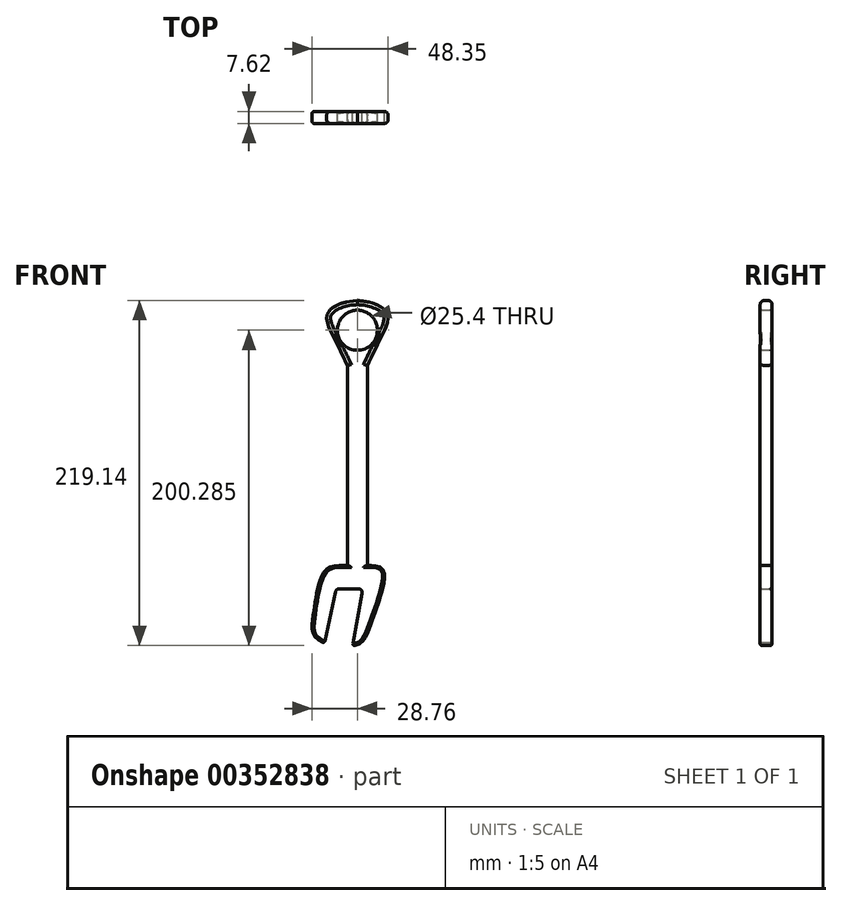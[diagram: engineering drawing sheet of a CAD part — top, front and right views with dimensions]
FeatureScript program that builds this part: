
annotation { "Feature Type Name" : "Feature", "Feature Type Description" : "" }
export const myFeature = defineFeature(function(context is Context, id is Id, definition is map)
    precondition{}
    {
        {
            var Q0;
            Q0=qCreatedBy(makeId("Front.planeOp"),FACE);
            var sketch = newSketch(context, id + "F0", { "sketchPlane" : qUnion([Q0])});
            skLineSegment(sketch, "E0.bottom", {"start": v(-6.35, 63.5) * mm, "end": v(6.35, 63.5) * mm});
            skLineSegment(sketch, "E0.top", {"start": v(-6.35, -63.5) * mm, "end": v(6.35, -63.5) * mm});
            skLineSegment(sketch, "E0.left", {"start": v(-6.35, 63.5) * mm, "end": v(-6.35, -63.5) * mm});
            skLineSegment(sketch, "E0.right", {"start": v(6.35, 63.5) * mm, "end": v(6.35, -63.5) * mm});
            skPoint(sketch, "E0.middle", {"position": v(0, 0) * mm});
            skLineSegment(sketch, "E1", {"start": v(-20.84, -113.07) * mm, "end": v(-13.93, -80.42) * mm});
            skLineSegment(sketch, "E2", {"start": v(-11.44, -78.4) * mm, "end": v(0.55, -78.4) * mm});
            skLineSegment(sketch, "E3", {"start": v(3.04, -81.41) * mm, "end": v(-3.28, -114.85) * mm});
            skFitSpline(sketch, "E4", {"points": [v(-3.28, -114.85) * mm, v(2.72, -112.4) * mm, v(10.94, -94.4) * mm, v(16.5, -66.62) * mm, v(6.35, -63.5) * mm], "startDerivative": vector(38.66, 7.37) * mm, "endDerivative": vector(-61.43, 0.88) * mm});
            skFitSpline(sketch, "E5", {"points": [v(-6.35, -63.5) * mm, v(-19.73, -66.18) * mm, v(-25.95, -82.18) * mm, v(-28.4, -98.18) * mm, v(-27.73, -107.96) * mm, v(-20.84, -113.07) * mm], "startDerivative": vector(-73.53, 0.95) * mm, "endDerivative": vector(51.22, -25.64) * mm});
            skPoint(sketch, "E6.visualSharp", {"position": v(-13.5, -78.4) * mm});
            skArc(sketch, "E6.filletArc", {"start": v(-11.44, -78.4) * mm, "mid": v(-13.04, -78.97) * mm, "end": v(-13.93, -80.42) * mm});
            skPoint(sketch, "E7.visualSharp", {"position": v(3.61, -78.4) * mm});
            skArc(sketch, "E7.filletArc", {"start": v(3.04, -81.41) * mm, "mid": v(2.5, -79.32) * mm, "end": v(0.55, -78.4) * mm});
            skFitSpline(sketch, "E8", {"points": [v(6.35, 63.5) * mm, v(15.43, 82.06) * mm, v(19.27, 95.82) * mm, v(10.3, 102.76) * mm, v(0, 104.65) * mm], "startDerivative": vector(29.74, 61.4) * mm, "endDerivative": vector(-46.2, 4.39) * mm});
            skFitSpline(sketch, "E9.MirrorCS", {"points": [v(-6.35, 63.5) * mm, v(-15.43, 82.06) * mm, v(-19.27, 95.82) * mm, v(-10.3, 102.76) * mm, v(0, 104.65) * mm], "startDerivative": vector(-29.74, 61.4) * mm, "endDerivative": vector(46.2, 4.39) * mm});
            skCircle(sketch, "E10", {"center": v(0, 85.8) * mm, "radius": 12.7 * mm});
            skSolve(sketch);
        }
        {
            var Q0;
            Q0=makeQuery(id+"F0.imprint","IMPRINT",FACE,{"disambiguationData":[TD([[makeQuery(id+"F0.imprint","IMPRINT",EDGE,{"derivedFrom":sQuery(id+"F0.wireOp",EDGE,"E0.bottom")}),1.0]])]});
            var Q1;
            Q1=makeQuery(id+"F0.imprint","IMPRINT",FACE,{"disambiguationData":[TD([[makeQuery(id+"F0.imprint","IMPRINT",EDGE,{"derivedFrom":sQuery(id+"F0.wireOp",EDGE,"E0.bottom")}),-1.0]])]});
            var Q2;
            Q2=makeQuery(id+"F0.imprint","IMPRINT",FACE,{"disambiguationData":[TD([[makeQuery(id+"F0.imprint","IMPRINT",EDGE,{"derivedFrom":sQuery(id+"F0.wireOp",EDGE,"E0.top")}),-1.0]])]});
            extrude(context, id + "F1", {"entities" : qUnion([Q0, Q1, Q2]), "depth" : 7.62 * mm});
        }
        {
            var Q0;
            Q0=makeQuery(id+"F1.opExtrude","CAP_EDGE",EDGE,{"disambiguationData":[OSD([sQuery(id+"F0.wireOp",EDGE,"E0.left")])],"isStart":false});
            var Q1;
            Q1=makeQuery(id+"F1.opExtrude","CAP_EDGE",EDGE,{"disambiguationData":[OSD([sQuery(id+"F0.wireOp",EDGE,"E0.right")])],"isStart":false});
            var Q2;
            Q2=makeQuery(id+"F1.opExtrude","CAP_EDGE",EDGE,{"disambiguationData":[OSD([sQuery(id+"F0.wireOp",EDGE,"E0.right")])],"isStart":true});
            var Q3;
            Q3=makeQuery(id+"F1.opExtrude","CAP_EDGE",EDGE,{"disambiguationData":[OSD([sQuery(id+"F0.wireOp",EDGE,"E0.left")])],"isStart":true});
            fillet(context, id + "F2", {"entities" : qUnion([Q0, Q1, Q2, Q3]), "radius" : 2.54 * mm, "tangentPropagation" : true, "allowEdgeOverflow" : false});
        }
        {
            var Q0;
            Q0=makeQuery(id+"F1.opExtrude","CAP_EDGE",EDGE,{"disambiguationData":[OSD([sQuery(id+"F0.wireOp",EDGE,"E5")])],"isStart":true});
            var Q1;
            Q1=makeQuery(id+"F1.opExtrude","CAP_EDGE",EDGE,{"disambiguationData":[OSD([sQuery(id+"F0.wireOp",EDGE,"E5")])],"isStart":false});
            var Q2;
            Q2=makeQuery(id+"F1.opExtrude","CAP_EDGE",EDGE,{"disambiguationData":[OSD([sQuery(id+"F0.wireOp",EDGE,"E4")])],"isStart":false});
            var Q3;
            Q3=makeQuery(id+"F1.opExtrude","CAP_EDGE",EDGE,{"disambiguationData":[OSD([sQuery(id+"F0.wireOp",EDGE,"E4")])],"isStart":true});
            var Q4;
            Q4=makeQuery(id+"F1.opExtrude","SWEPT_EDGE",EDGE,{"disambiguationData":[OSD([sQuery(id+"F0.wireOp",EDGE,"E1"),sQuery(id+"F0.wireOp",EDGE,"E5")])]});
            var Q5;
            Q5=makeQuery(id+"F1.opExtrude","SWEPT_EDGE",EDGE,{"disambiguationData":[OSD([sQuery(id+"F0.wireOp",EDGE,"E3"),sQuery(id+"F0.wireOp",EDGE,"E4")])]});
            var Q6;
            Q6=makeQuery(id+"F1.opExtrude","CAP_EDGE",EDGE,{"disambiguationData":[OSD([sQuery(id+"F0.wireOp",EDGE,"E2")])],"isStart":true});
            var Q7;
            Q7=makeQuery(id+"F1.opExtrude","CAP_EDGE",EDGE,{"disambiguationData":[OSD([sQuery(id+"F0.wireOp",EDGE,"E1")])],"isStart":false});
            var Q8;
            Q8=makeQuery(id+"F1.opExtrude","CAP_EDGE",EDGE,{"disambiguationData":[OSD([sQuery(id+"F0.wireOp",EDGE,"E1")])],"isStart":true});
            fillet(context, id + "F3", {"entities" : qUnion([Q0, Q1, Q2, Q3, Q4, Q5, Q6, Q7, Q8]), "radius" : 1.27 * mm, "tangentPropagation" : true, "allowEdgeOverflow" : false});
        }
        {
            var Q0;
            Q0=makeQuery(id+"F1.opExtrude","CAP_EDGE",EDGE,{"disambiguationData":[OSD([sQuery(id+"F0.wireOp",EDGE,"E9.MirrorCS")])],"isStart":false});
            var Q1;
            Q1=makeQuery(id+"F1.opExtrude","CAP_EDGE",EDGE,{"disambiguationData":[OSD([sQuery(id+"F0.wireOp",EDGE,"E9.MirrorCS")])],"isStart":true});
            var Q2;
            Q2=makeQuery(id+"F1.opExtrude","CAP_EDGE",EDGE,{"disambiguationData":[OSD([sQuery(id+"F0.wireOp",EDGE,"E8")])],"isStart":false});
            var Q3;
            Q3=makeQuery(id+"F1.opExtrude","CAP_EDGE",EDGE,{"disambiguationData":[OSD([sQuery(id+"F0.wireOp",EDGE,"E8")])],"isStart":true});
            fillet(context, id + "F4", {"entities" : qUnion([Q0, Q1, Q2, Q3]), "radius" : 2.54 * mm, "tangentPropagation" : true, "allowEdgeOverflow" : false});
        }
        {
            var Q0;
            Q0=makeQuery(id+"F1.opExtrude","CAP_EDGE",EDGE,{"disambiguationData":[OSD([sQuery(id+"F0.wireOp",EDGE,"E10")])],"isStart":false});
            var Q1;
            Q1=makeQuery(id+"F1.opExtrude","CAP_EDGE",EDGE,{"disambiguationData":[OSD([sQuery(id+"F0.wireOp",EDGE,"E10")])],"isStart":true});
            fillet(context, id + "F5", {"entities" : qUnion([Q0, Q1]), "radius" : 1.02 * mm, "tangentPropagation" : true, "allowEdgeOverflow" : false});
        }
    });
